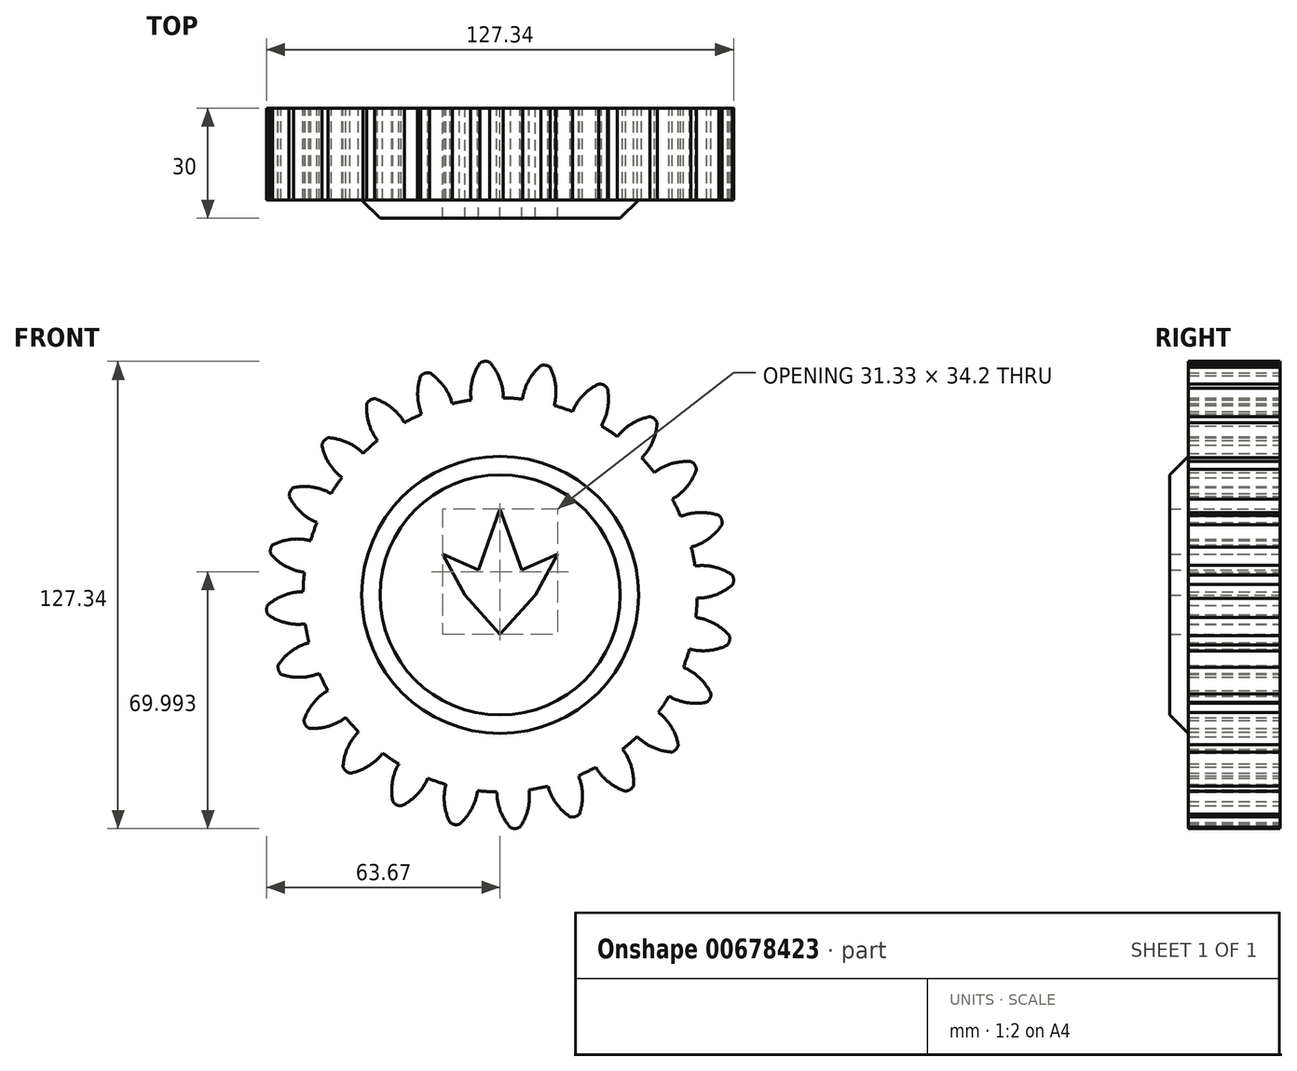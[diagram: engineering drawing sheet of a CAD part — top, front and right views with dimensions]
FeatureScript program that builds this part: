
annotation { "Feature Type Name" : "Feature", "Feature Type Description" : "" }
export const myFeature = defineFeature(function(context is Context, id is Id, definition is map)
    precondition{}
    {
        {
            var Q0;
            Q0=qCreatedBy(makeId("Front.planeOp"),FACE);
            var sketch = newSketch(context, id + "F0", { "sketchPlane" : qUnion([Q0])});
            skCircle(sketch, "E0", {"center": v(0, 0) * mm, "radius": 53.72 * mm});
            skCircle(sketch, "E1", {"center": v(0, 0) * mm, "radius": 58.67 * mm, "construction": true});
            skCircle(sketch, "E2", {"center": v(0, 0) * mm, "radius": 63.5 * mm, "construction": true});
            skLineSegment(sketch, "E3", {"start": v(0, 0) * mm, "end": v(0, 159.95) * mm, "construction": true});
            skLineSegment(sketch, "E4", {"start": v(0, 0) * mm, "end": v(-12.76, 194.75) * mm, "construction": true});
            skLineSegment(sketch, "E5", {"start": v(0, 58.67) * mm, "end": v(-65.03, 58.67) * mm, "construction": true});
            skLineSegment(sketch, "E6", {"start": v(0, 58.67) * mm, "end": v(-68.02, 33.92) * mm, "construction": true});
            skCircle(sketch, "E7", {"center": v(0, 0) * mm, "radius": 55.14 * mm, "construction": true});
            skCircle(sketch, "E8", {"center": v(0, 58.67) * mm, "radius": 14.6 * mm, "construction": true});
            skCircle(sketch, "E9", {"center": v(-13.72, 53.68) * mm, "radius": 14.6 * mm, "construction": true});
            skArc(sketch, "E10", {"start": v(0, 58.67) * mm, "mid": v(-1.2, 61.19) * mm, "end": v(-2.86, 63.44) * mm});
            skArc(sketch, "E11", {"start": v(0.88, 53.71) * mm, "mid": v(0.66, 56.23) * mm, "end": v(0, 58.67) * mm});
            skArc(sketch, "E12.MirrorCS", {"start": v(-7.66, 58.17) * mm, "mid": v(-6.8, 60.82) * mm, "end": v(-5.45, 63.27) * mm});
            skArc(sketch, "E13.MirrorCS", {"start": v(-7.88, 53.14) * mm, "mid": v(-8, 55.67) * mm, "end": v(-7.66, 58.17) * mm});
            skArc(sketch, "E14", {"start": v(-2.86, 63.44) * mm, "mid": v(-4.17, 63.67) * mm, "end": v(-5.45, 63.27) * mm});
            skCircle(sketch, "E15", {"center": v(0, 0) * mm, "radius": 37.75 * mm});
            skLineSegment(sketch, "E16", {"start": v(-9.63, 0) * mm, "end": v(-15.66, 11.07) * mm});
            skLineSegment(sketch, "E17", {"start": v(-15.66, 11.07) * mm, "end": v(-5.9, 6.75) * mm});
            skLineSegment(sketch, "E18", {"start": v(-5.9, 6.75) * mm, "end": v(0, 23.42) * mm});
            skLineSegment(sketch, "E19", {"start": v(-9.63, 0) * mm, "end": v(0, -10.78) * mm});
            skLineSegment(sketch, "E20.MirrorCS", {"start": v(5.9, 6.75) * mm, "end": v(0, 23.42) * mm});
            skLineSegment(sketch, "E21.MirrorCS", {"start": v(15.66, 11.07) * mm, "end": v(5.9, 6.75) * mm});
            skLineSegment(sketch, "E22.MirrorCS", {"start": v(9.63, 0) * mm, "end": v(15.66, 11.07) * mm});
            skLineSegment(sketch, "E23.MirrorCS", {"start": v(9.63, 0) * mm, "end": v(0, -10.78) * mm});
            skSolve(sketch);
        }
        {
            var Q0;
            Q0=makeQuery(id+"F0.imprint","IMPRINT",FACE,{"disambiguationData":[TD([[makeQuery(id+"F0.imprint","IMPRINT",EDGE,{"derivedFrom":sQuery(id+"F0.wireOp",EDGE,"E10")}),1.0]])]});
            var Q1;
            Q1=makeQuery(id+"F0.imprint","IMPRINT",FACE,{"disambiguationData":[TD([[makeQuery(id+"F0.imprint","IMPRINT",EDGE,{"derivedFrom":sQuery(id+"F0.wireOp",EDGE,"E15")}),-1.0]])]});
            extrude(context, id + "F1", {"entities" : qUnion([Q0, Q1]), "depth" : 25 * mm, "offsetDistance" : 25 * mm});
        }
        {
            var Q0;
            Q0=makeQuery(id+"F1.opExtrude","SWEPT_BODY",BODY,{"disambiguationData":[OSD([sQuery(id+"F0.wireOp",EDGE,"E0"),sQuery(id+"F0.wireOp",EDGE,"E10"),sQuery(id+"F0.wireOp",EDGE,"E11"),sQuery(id+"F0.wireOp",EDGE,"E12.MirrorCS"),sQuery(id+"F0.wireOp",EDGE,"E13.MirrorCS"),sQuery(id+"F0.wireOp",EDGE,"E14")])]});
            var Q1;
            Q1=makeQuery(id+"F1.opExtrude","SWEPT_FACE",FACE,{"disambiguationData":[OSD([sQuery(id+"F0.wireOp",EDGE,"E0")])]});
            circularPattern(context, id + "F2", {"entities" : qUnion([Q0]), "axis" : qUnion([Q1]), "angle" : 360 * degree, "instanceCount" : 24, "equalSpace" : true});
        }
        {
            var Q0;
            Q0=makeQuery(id+"F0.imprint","IMPRINT",FACE,{"disambiguationData":[TD([[makeQuery(id+"F0.imprint","IMPRINT",EDGE,{"derivedFrom":sQuery(id+"F0.wireOp",EDGE,"E15")}),1.0]])]});
            extrude(context, id + "F3", {"entities" : qUnion([Q0]), "operationType" : NewBodyOperationType.ADD, "depth" : 30 * mm, "offsetDistance" : 25 * mm});
        }
        {
            var Q0;
            Q0=makeQuery(id+"F3.opExtrude","CAP_EDGE",EDGE,{"disambiguationData":[OSD([sQuery(id+"F0.wireOp",EDGE,"E15")])],"isStart":false});
            var Q1;
            Q1=makeQuery(id+"F3.opExtrude","CAP_EDGE",EDGE,{"disambiguationData":[OSD([sQuery(id+"F0.wireOp",EDGE,"E15")])],"isStart":true});
            chamfer(context, id + "F4", {"entities" : qUnion([Q0, Q1]), "width" : 5 * mm, "tangentPropagation" : true});
        }
    });
